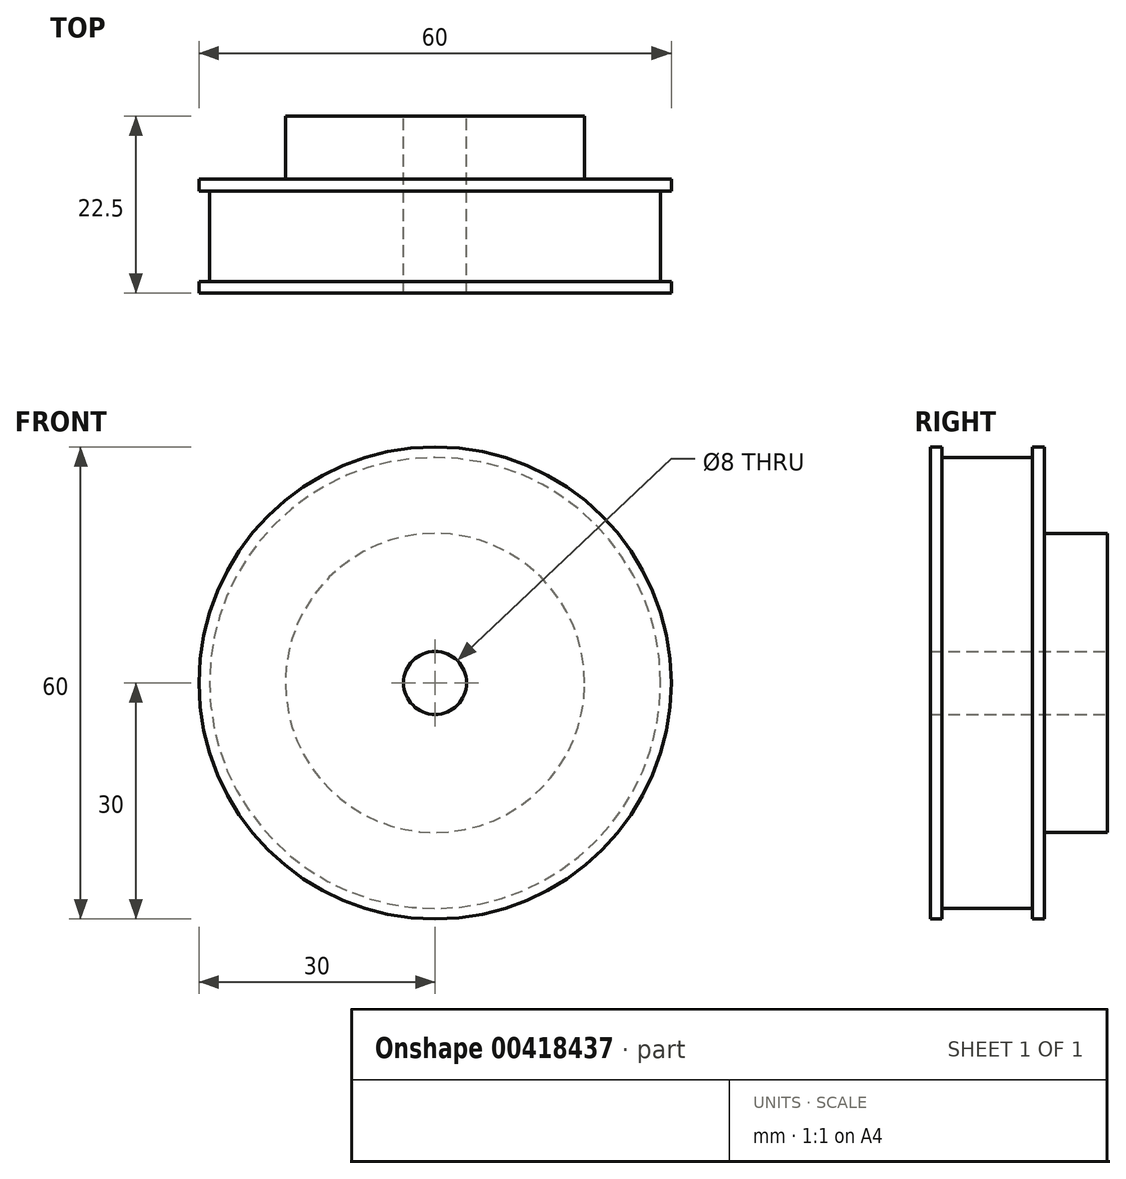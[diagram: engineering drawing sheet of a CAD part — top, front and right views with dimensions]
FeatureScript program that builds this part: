
annotation { "Feature Type Name" : "Feature", "Feature Type Description" : "" }
export const myFeature = defineFeature(function(context is Context, id is Id, definition is map)
    precondition{}
    {
        {
            var Q0;
            Q0=qCreatedBy(makeId("Front.planeOp"),FACE);
            var sketch = newSketch(context, id + "F0", { "sketchPlane" : qUnion([Q0])});
            skCircle(sketch, "E0", {"center": v(0, 0) * mm, "radius": 30 * mm});
            skSolve(sketch);
        }
        {
            var Q0;
            Q0=qSketchRegion(id+"F0",true);
            extrude(context, id + "F1", {"entities" : qUnion([Q0]), "depth" : 1.5 * mm});
        }
        {
            var Q0;
            Q0=makeQuery(id+"F1.opExtrude","CAP_FACE",FACE,{"disambiguationData":[OSD([sQuery(id+"F0.wireOp",EDGE,"E0")])],"isStart":true});
            var sketch = newSketch(context, id + "F2", { "sketchPlane" : qUnion([Q0])});
            skCircle(sketch, "E1", {"center": v(0, 0) * mm, "radius": 28.65 * mm});
            skSolve(sketch);
        }
        {
            var Q0;
            Q0=qSketchRegion(id+"F2",true);
            extrude(context, id + "F3", {"entities" : qUnion([Q0]), "operationType" : NewBodyOperationType.ADD, "depth" : 11.5 * mm});
        }
        {
            var Q0;
            Q0=makeQuery(id+"F3.opExtrude","CAP_FACE",FACE,{"disambiguationData":[OSD([sQuery(id+"F2.wireOp",EDGE,"E1")])],"isStart":false});
            var sketch = newSketch(context, id + "F4", { "sketchPlane" : qUnion([Q0])});
            skCircle(sketch, "E2", {"center": v(0, 0) * mm, "radius": 30 * mm});
            skSolve(sketch);
        }
        {
            var Q0;
            Q0=qSketchRegion(id+"F4",true);
            extrude(context, id + "F5", {"entities" : qUnion([Q0]), "operationType" : NewBodyOperationType.ADD, "depth" : 1.5 * mm});
        }
        {
            var Q0;
            Q0=makeQuery(id+"F5.opExtrude","CAP_FACE",FACE,{"disambiguationData":[OSD([sQuery(id+"F4.wireOp",EDGE,"E2")])],"isStart":false});
            var sketch = newSketch(context, id + "F6", { "sketchPlane" : qUnion([Q0])});
            skCircle(sketch, "E3", {"center": v(0, 0) * mm, "radius": 19 * mm});
            skSolve(sketch);
        }
        {
            var Q0;
            Q0=qSketchRegion(id+"F6",true);
            extrude(context, id + "F7", {"entities" : qUnion([Q0]), "operationType" : NewBodyOperationType.ADD, "depth" : (22.5 - 14.5) * mm});
        }
        {
            var Q0;
            Q0=makeQuery(id+"F7.opExtrude","CAP_FACE",FACE,{"disambiguationData":[OSD([sQuery(id+"F6.wireOp",EDGE,"E3")])],"isStart":false});
            var sketch = newSketch(context, id + "F8", { "sketchPlane" : qUnion([Q0])});
            skCircle(sketch, "E4", {"center": v(0, 0) * mm, "radius": 4 * mm});
            skSolve(sketch);
        }
        {
            var Q0;
            Q0=qSketchRegion(id+"F8",true);
            extrude(context, id + "F9", {"entities" : qUnion([Q0]), "operationType" : NewBodyOperationType.REMOVE, "endBound" : BoundingType.THROUGH_ALL, "oppositeDirection" : true, "depth" : 25 * mm});
        }
    });
